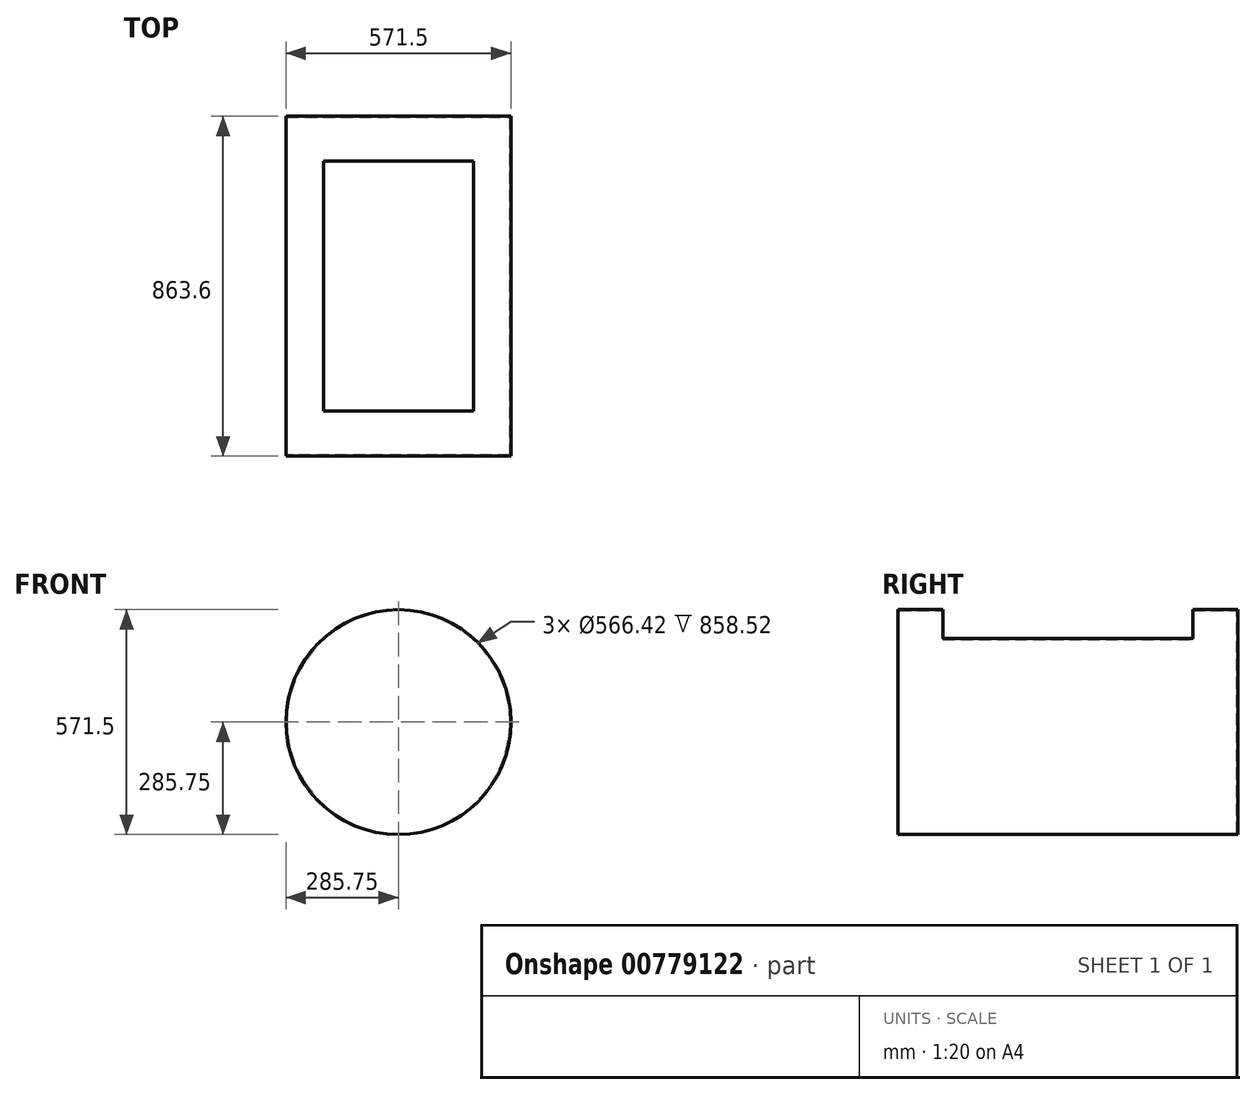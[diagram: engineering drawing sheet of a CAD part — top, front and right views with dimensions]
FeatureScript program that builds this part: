
annotation { "Feature Type Name" : "Feature", "Feature Type Description" : "" }
export const myFeature = defineFeature(function(context is Context, id is Id, definition is map)
    precondition{}
    {
        {
            var Q0;
            Q0=qCreatedBy(makeId("Front.planeOp"),FACE);
            var sketch = newSketch(context, id + "F0", { "sketchPlane" : qUnion([Q0])});
            skCircle(sketch, "E0", {"center": v(0, 0) * mm, "radius": 285.75 * mm});
            skSolve(sketch);
        }
        {
            var Q0;
            Q0 = qSketchRegion(id + "F0", true);
            extrude(context, id + "F1", {"entities" : qUnion([Q0]), "endBound" : BoundingType.SYMMETRIC, "depth" : 863.6 * mm, "offsetDistance" : 25.4 * mm});
        }
        {
            var Q0;
            Q0=qCreatedBy(makeId("Top.planeOp"),FACE);
            var sketch = newSketch(context, id + "F2", { "sketchPlane" : qUnion([Q0])});
            skLineSegment(sketch, "E1.bottom", {"start": v(-190.5, 317.5) * mm, "end": v(190.5, 317.5) * mm});
            skLineSegment(sketch, "E1.top", {"start": v(-190.5, -317.5) * mm, "end": v(190.5, -317.5) * mm});
            skLineSegment(sketch, "E1.left", {"start": v(-190.5, 317.5) * mm, "end": v(-190.5, -317.5) * mm});
            skLineSegment(sketch, "E1.right", {"start": v(190.5, 317.5) * mm, "end": v(190.5, -317.5) * mm});
            skPoint(sketch, "E1.middle", {"position": v(0, 0) * mm});
            skSolve(sketch);
        }
        {
            var Q0;
            Q0 = qSketchRegion(id + "F2", true);
            extrude(context, id + "F3", {"entities" : qUnion([Q0]), "operationType" : NewBodyOperationType.REMOVE, "depth" : 452.12 * mm, "offsetDistance" : 25.4 * mm});
        }
        {
            var Q0;
            Q0=makeQuery(id+"F3.boolean.opBoolean","COPY",FACE,{"derivedFrom":makeQuery(id+"F3.opExtrude","SWEPT_FACE",FACE,{"disambiguationData":[OSD([sQuery(id+"F2.wireOp",EDGE,"E1.bottom")])]})});
            var Q1;
            Q1=makeQuery(id+"F3.boolean.opBoolean","COPY",FACE,{"derivedFrom":makeQuery(id+"F3.opExtrude","SWEPT_FACE",FACE,{"disambiguationData":[OSD([sQuery(id+"F2.wireOp",EDGE,"E1.left")])]})});
            var Q2;
            Q2=makeQuery(id+"F3.boolean.opBoolean","COPY",FACE,{"derivedFrom":makeQuery(id+"F3.opExtrude","CAP_FACE",FACE,{"disambiguationData":[OSD([sQuery(id+"F2.wireOp",EDGE,"E1.bottom"),sQuery(id+"F2.wireOp",EDGE,"E1.top"),sQuery(id+"F2.wireOp",EDGE,"E1.left"),sQuery(id+"F2.wireOp",EDGE,"E1.right")])],"isStart":true})});
            var Q3;
            Q3=makeQuery(id+"F3.boolean.opBoolean","COPY",FACE,{"derivedFrom":makeQuery(id+"F3.opExtrude","SWEPT_FACE",FACE,{"disambiguationData":[OSD([sQuery(id+"F2.wireOp",EDGE,"E1.top")])]})});
            var Q4;
            Q4=makeQuery(id+"F3.boolean.opBoolean","COPY",FACE,{"derivedFrom":makeQuery(id+"F3.opExtrude","SWEPT_FACE",FACE,{"disambiguationData":[OSD([sQuery(id+"F2.wireOp",EDGE,"E1.right")])]})});
            shell(context, id + "F4", {"entities" : qUnion([Q0, Q1, Q2, Q3, Q4]), "thickness" : 2.54 * mm});
        }
    });
